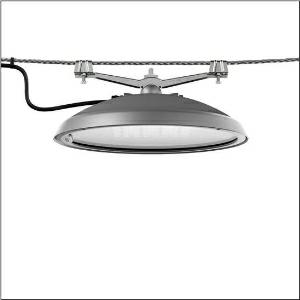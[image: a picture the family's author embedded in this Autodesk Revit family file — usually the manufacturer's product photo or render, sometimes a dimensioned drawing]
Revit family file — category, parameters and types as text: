
# Revit family: dl_50_iq_mini___st1_0s_5xa248w41f08he_9e8d
name_source: partatom
category: Lighting Fixtures
units: mm (PartAtom-declared; Revit-internal decimal feet)

## family parameters
Cut with Voids When Loaded = No
Host = Face
Light Source = No
Part Type = Normal
Room Calculation Point = No
Round Connector Dimension = Use Diameter
Shared = No

## types (1)
- --- (1 x LED, 9400 lm, 64.6 W, 4000K)
    Apparent Load = 65 VA
    CIE Flux Codes = 37 72 97 100 100
    Color Rendering = 70
    Color Temperature = 4000K
    Default Elevation = 1800 mm
    Description = DL 50 iQ mini, catenary luminaire, primary light control with lens, of PMMA, primary optical cover: cover, of toughened safety glass, transparent, light distribution: ST1.0s, light emission: direct distribution, primary light characteristic: symmetric, installation type: suspended mounting, LED, High Power LED, rated luminous flux: 9.400lm, luminous efficacy: 146lm/W, light colour: 740, colour temperature: 4000K, control gear: iQ Street-Remote, control: optimised constant luminous flux control (CLO 2.0), Desk-Remote (wireless, voltage-free reading and setting of iQ features in the workshop via application-optimized NFC function/RFID function), Light-Fading, Smart-Wire, Night-Set, Lumen-Switch, Temp-Guard, Auto-Match, Street-Remote, mains connection: 230..240V, AC, 50/60Hz, start of lifetime: 65W, end of service life: 68W, reduction: 29W, luminaire housing, of diecast aluminium, powder-coated, SITECO metallic grey (DB 702S), diameter: 500mm, height: 115mm, mounting height: 4..12m, protection rating (complete): IP66, insulation class (complete): insulation class II (safety insulation), certification: CE, ENEC, ENEC+, VDE, impact resistance: IK08, permissible operating ambient temperature for outdoor applications: -25..+40°C, standard-compliant lighting for roads and squares, packaging unit: 1 piece

Light Distribution: ST1.0s
    Height = 124 mm  [stored 0.406824 ft]
    Lamp = 1 x LED
    Lamp Light Flux = 9400 lm
    Lamp Power = 64.6 W
    Lamp count = 1
    Length = 500 mm
    Luminous efficacy = 146 lm/W
    Manufacturer = Siteco
    ModVariant = No
    Model = 5XA248W41F08HE
    Number of Poles = 1
    OnlyDefault = Yes
    Power Factor = 1
    Product Name = DL 50 iQ mini | ST1.0s
    Product group = catenary luminaire
    ProductGroupID = 6300
    Protection Class = Protection class II
    Protection Degree = IP 66
    RLX_Detail_Level = 1
    RLX_Emergency_Light_Flux = 0 lm
    RLX_Emergency_Type = 0
    RLX_Emergency_Type_DB = No
    RlxData = <blob elided: 123481 chars, md5=e0a270c4>
    Socket = socket
    Standby Power = 0 W
    System Light Flux = 9400 lm
    System Power = 65 W
    Type Comments = factory setting: luminous flux: 100 % | dim-lin: 254 | 655 mA
    Type Image = l_1242791.jpg
    URL = http://relux.com
    VarID = @adj_140097
    Voltage = 0 V
    Weight = 0.00 kg
    Width = 0 mm  [stored 0 ft]

note: [stored X ft] marks values corroborated as IEEE doubles in the binary element streams (Revit-internal decimal feet)

## geometry (parser evidence)
native form markers: Blend x4, Sweep x12
no freeform markers — native parametric forms only
